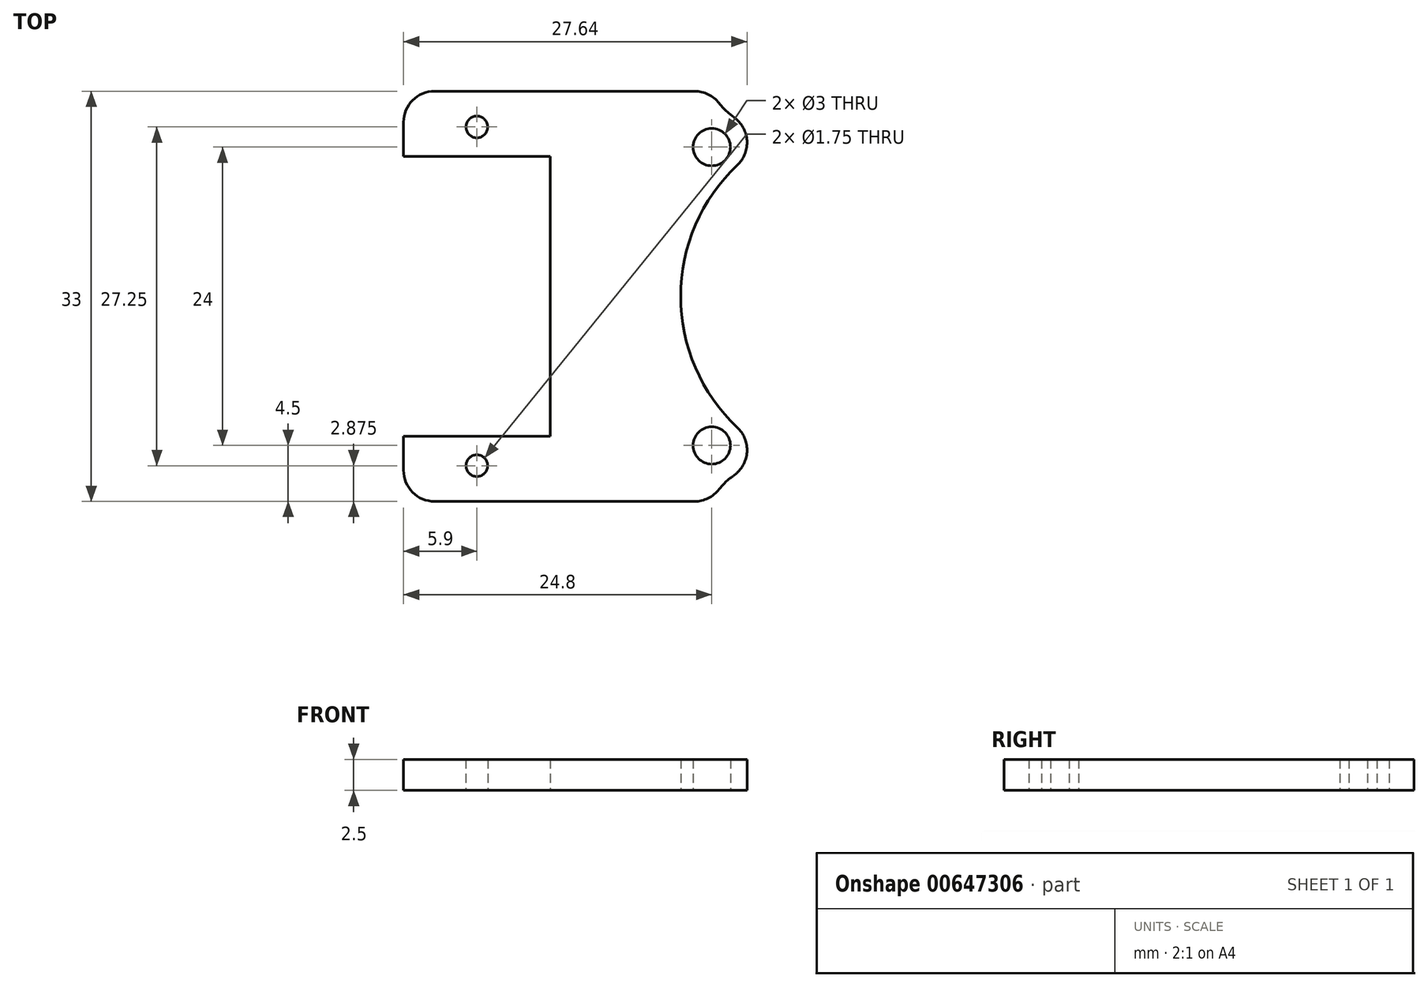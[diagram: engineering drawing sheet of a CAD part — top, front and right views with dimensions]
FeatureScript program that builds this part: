
annotation { "Feature Type Name" : "Feature", "Feature Type Description" : "" }
export const myFeature = defineFeature(function(context is Context, id is Id, definition is map)
    precondition{}
    {
        {
            var Q0;
            Q0=qCreatedBy(makeId("Top.planeOp"),FACE);
            var sketch = newSketch(context, id + "F0", { "sketchPlane" : qUnion([Q0])});
            skLineSegment(sketch, "E0.bottom", {"start": v(12, -15) * mm, "end": v(-12, -15) * mm});
            skLineSegment(sketch, "E0.top", {"start": v(12, 15) * mm, "end": v(-12, 15) * mm});
            skLineSegment(sketch, "E0.left", {"start": v(15, -12) * mm, "end": v(15, 12) * mm});
            skLineSegment(sketch, "E0.right", {"start": v(-15, -12) * mm, "end": v(-15, 12) * mm});
            skPoint(sketch, "E0.middle", {"position": v(0, 0) * mm});
            skCircle(sketch, "E1", {"center": v(12, 12) * mm, "radius": 1.5 * mm});
            skCircle(sketch, "E2", {"center": v(-12, -12) * mm, "radius": 1.5 * mm});
            skPoint(sketch, "E3.visualSharp", {"position": v(-15, 15) * mm});
            skArc(sketch, "E3.filletArc", {"start": v(-12, 15) * mm, "mid": v(-14.12, 14.12) * mm, "end": v(-15, 12) * mm});
            skPoint(sketch, "E4.visualSharp", {"position": v(15, 15) * mm});
            skArc(sketch, "E4.filletArc", {"start": v(15, 12) * mm, "mid": v(14.12, 14.12) * mm, "end": v(12, 15) * mm});
            skPoint(sketch, "E5.visualSharp", {"position": v(15, -15) * mm});
            skArc(sketch, "E5.filletArc", {"start": v(12, -15) * mm, "mid": v(14.12, -14.12) * mm, "end": v(15, -12) * mm});
            skPoint(sketch, "E6.visualSharp", {"position": v(-15, -15) * mm});
            skArc(sketch, "E6.filletArc", {"start": v(-15, -12) * mm, "mid": v(-14.12, -14.12) * mm, "end": v(-12, -15) * mm});
            skCircle(sketch, "E7", {"center": v(0, 0) * mm, "radius": 14.5 * mm});
            skLineSegment(sketch, "E8.bottom", {"start": v(-12, 15) * mm, "end": v(-46.8, 15) * mm});
            skLineSegment(sketch, "E8.top", {"start": v(-12, -15) * mm, "end": v(-46.8, -15) * mm});
            skLineSegment(sketch, "E8.right", {"start": v(-46.8, 15) * mm, "end": v(-46.8, -15) * mm});
            skCircle(sketch, "E9.MirrorC", {"center": v(-12, 12) * mm, "radius": 1.5 * mm});
            skCircle(sketch, "E10.MirrorC", {"center": v(12, -12) * mm, "radius": 1.5 * mm});
            skArc(sketch, "E11", {"start": v(-12, 15) * mm, "mid": v(-9.65, 13.86) * mm, "end": v(-9.08, 11.3) * mm});
            skArc(sketch, "E12", {"start": v(-12, -15) * mm, "mid": v(-9.65, -13.86) * mm, "end": v(-9.08, -11.3) * mm});
            skLineSegment(sketch, "E13", {"start": v(-46.8, 0) * mm, "end": v(-15, 0) * mm, "construction": true});
            skLineSegment(sketch, "E14.bottom", {"start": v(-25, -11.25) * mm, "end": v(-36.8, -11.25) * mm});
            skLineSegment(sketch, "E14.top", {"start": v(-25, 11.25) * mm, "end": v(-36.8, 11.25) * mm});
            skLineSegment(sketch, "E14.left", {"start": v(-25, -11.25) * mm, "end": v(-25, 11.25) * mm});
            skLineSegment(sketch, "E14.right", {"start": v(-36.8, -11.25) * mm, "end": v(-36.8, 11.25) * mm});
            skPoint(sketch, "E14.middle", {"position": v(-30.9, 0) * mm});
            skLineSegment(sketch, "E15", {"start": v(-30.9, 15) * mm, "end": v(-30.9, -15) * mm, "construction": true});
            skPoint(sketch, "E15.startSnap0", {"position": v(-30.9, -11.25) * mm});
            skCircle(sketch, "E16", {"center": v(-30.9, -13.63) * mm, "radius": 0.88 * mm});
            skCircle(sketch, "E17.MirrorC", {"center": v(-30.9, 13.62) * mm, "radius": 0.88 * mm});
            skLineSegment(sketch, "E18.left", {"start": v(-12, 15) * mm, "end": v(-12, 15) * mm});
            skPoint(sketch, "E18.middle", {"position": v(-46.8, 15) * mm});
            skLineSegment(sketch, "E19.bottom", {"start": v(-46.8, 15) * mm, "end": v(-12, 15) * mm});
            skLineSegment(sketch, "E19.top", {"start": v(-46.8, 16.5) * mm, "end": v(-12, 16.5) * mm});
            skLineSegment(sketch, "E19.left", {"start": v(-46.8, 15) * mm, "end": v(-46.8, 16.5) * mm});
            skLineSegment(sketch, "E19.right", {"start": v(-12, 15) * mm, "end": v(-12, 16.5) * mm});
            skLineSegment(sketch, "E20.bottom", {"start": v(-46.8, -15) * mm, "end": v(-12, -15) * mm});
            skLineSegment(sketch, "E20.top", {"start": v(-46.8, -16.5) * mm, "end": v(-12, -16.5) * mm});
            skLineSegment(sketch, "E20.left", {"start": v(-46.8, -15) * mm, "end": v(-46.8, -16.5) * mm});
            skLineSegment(sketch, "E20.right", {"start": v(-12, -15) * mm, "end": v(-12, -16.5) * mm});
            skLineSegment(sketch, "E21.bottom", {"start": v(-36.8, 16.5) * mm, "end": v(-40.3, 16.5) * mm});
            skLineSegment(sketch, "E21.top", {"start": v(-36.8, -16.5) * mm, "end": v(-40.3, -16.5) * mm});
            skLineSegment(sketch, "E21.left", {"start": v(-36.8, 16.5) * mm, "end": v(-36.8, -16.5) * mm});
            skLineSegment(sketch, "E21.right", {"start": v(-40.3, 16.5) * mm, "end": v(-40.3, -16.5) * mm});
            skSolve(sketch);
        }
        {
            var Q0;
            {var subQ0=sQuery(id+"F0.wireOp",EDGE,"E19.right");Q0=makeQuery(id+"F0.imprint","IMPRINT",FACE,{"disambiguationData":[TD([[makeQuery(id+"F0.imprint","IMPRINT",EDGE,{"derivedFrom":subQ0}),1.0]])]});}
            var Q1;
            {var subQ5=sQuery(id+"F0.wireOp",EDGE,"E21.bottom");Q1=makeQuery(id+"F0.imprint","IMPRINT",FACE,{"disambiguationData":[TD([[makeQuery(id+"F0.imprint","IMPRINT",EDGE,{"derivedFrom":subQ5}),1.0]])]});}
            var Q2;
            Q2=makeQuery(id+"F0.imprint","IMPRINT",FACE,{"disambiguationData":[TD([[makeQuery(id+"F0.imprint","IMPRINT",EDGE,{"derivedFrom":sQuery(id+"F0.wireOp",EDGE,"E0.right")}),1.0]])]});
            var Q3;
            Q3=makeQuery(id+"F0.imprint","IMPRINT",FACE,{"disambiguationData":[TD([[makeQuery(id+"F0.imprint","IMPRINT",EDGE,{"derivedFrom":sQuery(id+"F0.wireOp",EDGE,"E0.right")}),-1.0]])]});
            var Q4;
            {var subQ0=sQuery(id+"F0.wireOp",EDGE,"E20.right");Q4=makeQuery(id+"F0.imprint","IMPRINT",FACE,{"disambiguationData":[TD([[makeQuery(id+"F0.imprint","IMPRINT",EDGE,{"derivedFrom":subQ0}),-1.0]])]});}
            var Q5;
            {var subQ5=sQuery(id+"F0.wireOp",EDGE,"E21.top");Q5=makeQuery(id+"F0.imprint","IMPRINT",FACE,{"disambiguationData":[TD([[makeQuery(id+"F0.imprint","IMPRINT",EDGE,{"derivedFrom":subQ5}),-1.0]])]});}
            var Q6;
            {var subQ2=sQuery(id+"F0.wireOp",EDGE,"E19.bottom");var subQ5=sQuery(id+"F0.wireOp",EDGE,"E21.right");var subQ9=makeQuery(id+"F0.imprint","INTERSECT",VERTEX,{"derivedFrom":[subQ2,subQ5]});Q6=makeQuery(id+"F0.imprint","IMPRINT",FACE,{"disambiguationData":[TD([[makeQuery(id+"F0.imprint","IMPRINT",EDGE,{"disambiguationData":[TD([[subQ9,-1.0]])],"derivedFrom":subQ2}),-1.0]])]});}
            extrude(context, id + "F1", {"entities" : qUnion([Q0, Q1, Q2, Q3, Q4, Q5, Q6]), "depth" : 2.5 * mm, "offsetDistance" : 25 * mm});
        }
        {
            var Q0;
            Q0=makeQuery(id+"F1.opExtrude","SWEPT_EDGE",EDGE,{"disambiguationData":[OSD([sQuery(id+"F0.wireOp",EDGE,"E0.top"),sQuery(id+"F0.wireOp",EDGE,"E3.filletArc"),sQuery(id+"F0.wireOp",EDGE,"E11"),sQuery(id+"F0.wireOp",EDGE,"E19.bottom"),sQuery(id+"F0.wireOp",EDGE,"E19.right")])]});
            var Q1;
            Q1=makeQuery(id+"F1.opExtrude","SWEPT_EDGE",EDGE,{"disambiguationData":[OSD([sQuery(id+"F0.wireOp",EDGE,"E0.bottom"),sQuery(id+"F0.wireOp",EDGE,"E6.filletArc"),sQuery(id+"F0.wireOp",EDGE,"E12"),sQuery(id+"F0.wireOp",EDGE,"E20.bottom"),sQuery(id+"F0.wireOp",EDGE,"E20.right")])]});
            fillet(context, id + "F2", {"entities" : qUnion([Q0, Q1]), "radius" : 5 * mm, "tangentPropagation" : true, "allowEdgeOverflow" : false});
        }
        {
            var Q0;
            Q0=makeQuery(id+"F2.opFillet","BLEND_EDGE",EDGE,{"blendedFrom":[makeQuery(id+"F1.opExtrude","SWEPT_EDGE",EDGE,{"disambiguationData":[OSD([sQuery(id+"F0.wireOp",EDGE,"E0.top"),sQuery(id+"F0.wireOp",EDGE,"E3.filletArc"),sQuery(id+"F0.wireOp",EDGE,"E11"),sQuery(id+"F0.wireOp",EDGE,"E19.bottom"),sQuery(id+"F0.wireOp",EDGE,"E19.right")])]}),makeQuery(id+"F1.opExtrude","SWEPT_FACE",FACE,{"disambiguationData":[OSD([sQuery(id+"F0.wireOp",EDGE,"E19.top")])]})],"blendedInto":[makeQuery(id+"F1.opExtrude","SWEPT_FACE",FACE,{"disambiguationData":[OSD([sQuery(id+"F0.wireOp",EDGE,"E19.top")])]})]});
            var Q1;
            Q1=makeQuery(id+"F2.opFillet","BLEND_EDGE",EDGE,{"blendedFrom":[makeQuery(id+"F1.opExtrude","SWEPT_EDGE",EDGE,{"disambiguationData":[OSD([sQuery(id+"F0.wireOp",EDGE,"E0.bottom"),sQuery(id+"F0.wireOp",EDGE,"E6.filletArc"),sQuery(id+"F0.wireOp",EDGE,"E12"),sQuery(id+"F0.wireOp",EDGE,"E20.bottom"),sQuery(id+"F0.wireOp",EDGE,"E20.right")])]}),makeQuery(id+"F1.opExtrude","SWEPT_FACE",FACE,{"disambiguationData":[OSD([sQuery(id+"F0.wireOp",EDGE,"E20.top")])]})],"blendedInto":[makeQuery(id+"F1.opExtrude","SWEPT_FACE",FACE,{"disambiguationData":[OSD([sQuery(id+"F0.wireOp",EDGE,"E20.top")])]})]});
            var Q2;
            Q2=makeQuery(id+"F1.opExtrude","SWEPT_EDGE",EDGE,{"disambiguationData":[OSD([sQuery(id+"F0.wireOp",EDGE,"E20.top"),sQuery(id+"F0.wireOp",EDGE,"E20.left")])]});
            var Q3;
            Q3=makeQuery(id+"F1.opExtrude","SWEPT_EDGE",EDGE,{"disambiguationData":[OSD([sQuery(id+"F0.wireOp",EDGE,"E19.top"),sQuery(id+"F0.wireOp",EDGE,"E19.left")])]});
            var Q4;
            Q4=makeQuery(id+"F1.opExtrude","SWEPT_EDGE",EDGE,{"disambiguationData":[OSD([sQuery(id+"F0.wireOp",EDGE,"E7"),sQuery(id+"F0.wireOp",EDGE,"E11")])]});
            var Q5;
            Q5=makeQuery(id+"F1.opExtrude","SWEPT_EDGE",EDGE,{"disambiguationData":[OSD([sQuery(id+"F0.wireOp",EDGE,"E7"),sQuery(id+"F0.wireOp",EDGE,"E12")])]});
            var Q6;
            Q6=makeQuery(id+"F1.opExtrude","SWEPT_EDGE",EDGE,{"disambiguationData":[OSD([sQuery(id+"F0.wireOp",EDGE,"E19.top"),sQuery(id+"F0.wireOp",EDGE,"E21.bottom"),sQuery(id+"F0.wireOp",EDGE,"E21.right")])]});
            var Q7;
            Q7=makeQuery(id+"F1.opExtrude","SWEPT_EDGE",EDGE,{"disambiguationData":[OSD([sQuery(id+"F0.wireOp",EDGE,"E20.top"),sQuery(id+"F0.wireOp",EDGE,"E21.top"),sQuery(id+"F0.wireOp",EDGE,"E21.right")])]});
            fillet(context, id + "F3", {"entities" : qUnion([Q0, Q1, Q2, Q3, Q4, Q5, Q6, Q7]), "radius" : 2.5 * mm, "tangentPropagation" : true, "allowEdgeOverflow" : false});
        }
    });
